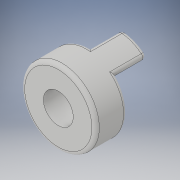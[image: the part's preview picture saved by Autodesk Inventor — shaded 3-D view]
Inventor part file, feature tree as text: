
AUTODESK INVENTOR PART (.ipt)
format: ipt  version: 2018 (Build 220112000, 112)  size: 212,992 bytes
history: native  units: in
note: dims shown in document units (in); Inventor stores cm internally (conversion verified against a paired STEP export)
features: extrude x2, fillet x2, sketch x1, pattern_circular x1
ambient origin geometry x8: Origin, YZ Plane, XZ Plane, XY Plane, X Axis, Y Axis, Z Axis, Center Point
bodies: Solid1 (feature_tree)
feature tree (6):
  sketch  "Sketch1"  dims[d0=0.625in d1=0.25in d2=45.0deg d3=0.05in d4=0.2656in d5=0.0in d6=0.2656in d7=0.0in d8=0.0312in d9=0.7874in d10=360.0deg d12=0.0312in]
  extrude  "Extrusion1"  Depth=0.0312in
  extrude  "Extrusion2"  TaperAngle=45.0deg  [1 undecoded]
  fillet  "Fillet1"  Radius=0.05in
  pattern_circular  "Circular Pattern1"  [2 undecoded]
  fillet  "Fillet2"  Radius=0.2656in
note: 3 required parameter values undecoded (feature->parameter linkage not recoverable at this tier; creation-order binding heuristic only, values carry confidence <= 0.55)
